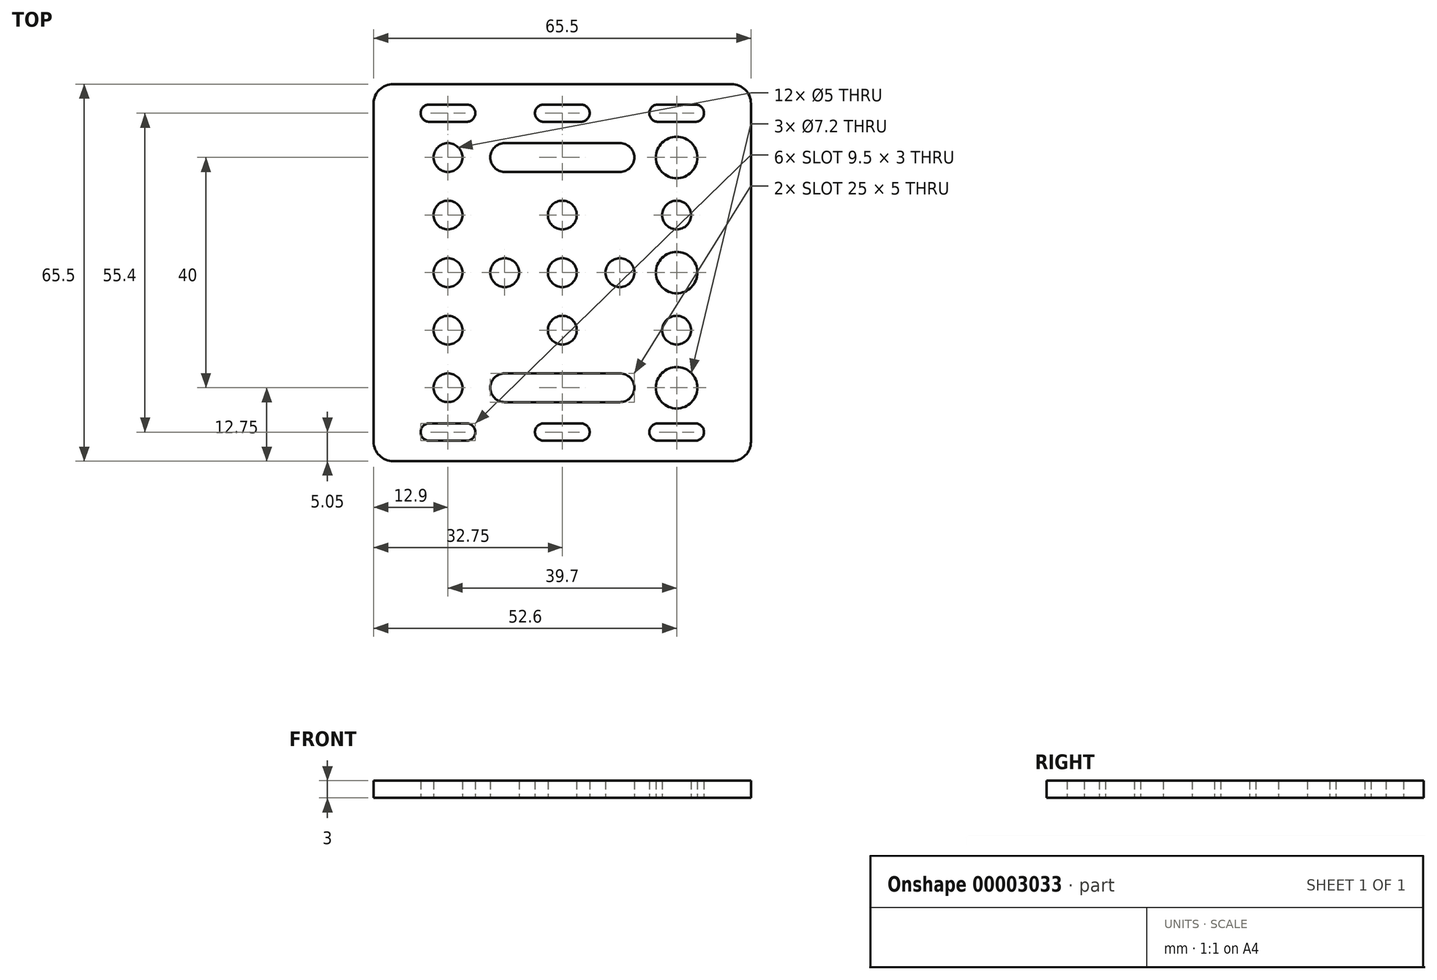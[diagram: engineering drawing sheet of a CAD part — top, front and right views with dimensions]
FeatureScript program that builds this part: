
annotation { "Feature Type Name" : "Feature", "Feature Type Description" : "" }
export const myFeature = defineFeature(function(context is Context, id is Id, definition is map)
    precondition{}
    {
        {
            var Q0;
            Q0=qCreatedBy(makeId("Top.planeOp"),FACE);
            var sketch = newSketch(context, id + "F0", { "sketchPlane" : qUnion([Q0])});
            skLineSegment(sketch, "E0.bottom", {"start": v(3.38, 0) * mm, "end": v(62.12, 0) * mm});
            skLineSegment(sketch, "E0.top", {"start": v(3.38, 65.5) * mm, "end": v(62.12, 65.5) * mm});
            skLineSegment(sketch, "E0.left", {"start": v(0, 3.38) * mm, "end": v(0, 62.12) * mm});
            skLineSegment(sketch, "E0.right", {"start": v(65.5, 3.38) * mm, "end": v(65.5, 62.12) * mm});
            skPoint(sketch, "E1.visualSharp", {"position": v(0, 65.5) * mm});
            skArc(sketch, "E1.filletArc", {"start": v(3.38, 65.5) * mm, "mid": v(0.99, 64.51) * mm, "end": v(0, 62.12) * mm});
            skPoint(sketch, "E2.visualSharp", {"position": v(0, 0) * mm});
            skArc(sketch, "E2.filletArc", {"start": v(0, 3.38) * mm, "mid": v(0.99, 0.99) * mm, "end": v(3.38, 0) * mm});
            skPoint(sketch, "E3.visualSharp", {"position": v(65.5, 0) * mm});
            skArc(sketch, "E3.filletArc", {"start": v(62.12, 0) * mm, "mid": v(64.51, 0.99) * mm, "end": v(65.5, 3.38) * mm});
            skPoint(sketch, "E4.visualSharp", {"position": v(65.5, 65.5) * mm});
            skArc(sketch, "E4.filletArc", {"start": v(65.5, 62.12) * mm, "mid": v(64.51, 64.51) * mm, "end": v(62.12, 65.5) * mm});
            skLineSegment(sketch, "E5", {"start": v(0, 32.75) * mm, "end": v(65.5, 32.75) * mm, "construction": true});
            skCircle(sketch, "E6", {"center": v(12.9, 32.75) * mm, "radius": 2.5 * mm});
            skCircle(sketch, "E7", {"center": v(22.75, 32.75) * mm, "radius": 2.5 * mm});
            skCircle(sketch, "E8", {"center": v(32.75, 32.75) * mm, "radius": 2.5 * mm});
            skCircle(sketch, "E9", {"center": v(52.6, 32.75) * mm, "radius": 3.6 * mm});
            skLineSegment(sketch, "E10", {"start": v(32.75, 65.5) * mm, "end": v(32.75, 0) * mm, "construction": true});
            skCircle(sketch, "E11", {"center": v(42.75, 32.75) * mm, "radius": 2.5 * mm});
            skCircle(sketch, "E12", {"center": v(12.9, 22.75) * mm, "radius": 2.5 * mm});
            skCircle(sketch, "E13", {"center": v(12.9, 12.75) * mm, "radius": 2.5 * mm});
            skCircle(sketch, "E14", {"center": v(32.75, 22.75) * mm, "radius": 2.5 * mm});
            skArc(sketch, "E15", {"start": v(22.75, 15.25) * mm, "mid": v(20.25, 12.75) * mm, "end": v(22.75, 10.25) * mm});
            skArc(sketch, "E16", {"start": v(42.75, 10.25) * mm, "mid": v(45.25, 12.75) * mm, "end": v(42.75, 15.25) * mm});
            skLineSegment(sketch, "E17", {"start": v(22.75, 15.25) * mm, "end": v(42.75, 15.25) * mm});
            skLineSegment(sketch, "E18", {"start": v(22.75, 10.25) * mm, "end": v(42.75, 10.25) * mm});
            skCircle(sketch, "E19", {"center": v(52.6, 12.75) * mm, "radius": 3.6 * mm});
            skCircle(sketch, "E20", {"center": v(52.6, 22.75) * mm, "radius": 2.5 * mm});
            skArc(sketch, "E21", {"start": v(9.65, 6.55) * mm, "mid": v(8.15, 5.05) * mm, "end": v(9.65, 3.55) * mm});
            skArc(sketch, "E22", {"start": v(16.15, 3.55) * mm, "mid": v(17.65, 5.05) * mm, "end": v(16.15, 6.55) * mm});
            skLineSegment(sketch, "E23", {"start": v(9.65, 6.55) * mm, "end": v(16.15, 6.55) * mm});
            skLineSegment(sketch, "E24", {"start": v(9.65, 3.55) * mm, "end": v(16.15, 3.55) * mm});
            skLineSegment(sketch, "E25.0.MirrorCS", {"start": v(55.85, 6.55) * mm, "end": v(49.35, 6.55) * mm});
            skArc(sketch, "E26.0.MirrorCS", {"start": v(49.35, 3.55) * mm, "mid": v(47.85, 5.05) * mm, "end": v(49.35, 6.55) * mm});
            skLineSegment(sketch, "E27.0.MirrorCS", {"start": v(55.85, 3.55) * mm, "end": v(49.35, 3.55) * mm});
            skArc(sketch, "E28.0.MirrorCS", {"start": v(55.85, 6.55) * mm, "mid": v(57.35, 5.05) * mm, "end": v(55.85, 3.55) * mm});
            skArc(sketch, "E29", {"start": v(29.5, 6.55) * mm, "mid": v(28, 5.05) * mm, "end": v(29.5, 3.55) * mm});
            skArc(sketch, "E30", {"start": v(36, 3.55) * mm, "mid": v(37.5, 5.05) * mm, "end": v(36, 6.55) * mm});
            skLineSegment(sketch, "E31", {"start": v(29.5, 6.55) * mm, "end": v(36, 6.55) * mm});
            skLineSegment(sketch, "E32", {"start": v(29.5, 3.55) * mm, "end": v(36, 3.55) * mm});
            skCircle(sketch, "E33.0.MirrorC", {"center": v(12.9, 42.75) * mm, "radius": 2.5 * mm});
            skCircle(sketch, "E34.0.MirrorC", {"center": v(32.75, 42.75) * mm, "radius": 2.5 * mm});
            skCircle(sketch, "E35.0.MirrorC", {"center": v(52.6, 42.75) * mm, "radius": 2.5 * mm});
            skCircle(sketch, "E36.0.MirrorC", {"center": v(52.6, 52.75) * mm, "radius": 3.6 * mm});
            skLineSegment(sketch, "E37.0.MirrorCS", {"start": v(22.75, 55.25) * mm, "end": v(42.75, 55.25) * mm});
            skArc(sketch, "E38.0.MirrorCS", {"start": v(42.75, 55.25) * mm, "mid": v(45.25, 52.75) * mm, "end": v(42.75, 50.25) * mm});
            skLineSegment(sketch, "E39.0.MirrorCS", {"start": v(22.75, 50.25) * mm, "end": v(42.75, 50.25) * mm});
            skArc(sketch, "E40.0.MirrorCS", {"start": v(22.75, 50.25) * mm, "mid": v(20.25, 52.75) * mm, "end": v(22.75, 55.25) * mm});
            skLineSegment(sketch, "E41.0.MirrorCS", {"start": v(9.65, 58.95) * mm, "end": v(16.15, 58.95) * mm});
            skArc(sketch, "E42.0.MirrorCS", {"start": v(16.15, 61.95) * mm, "mid": v(17.65, 60.45) * mm, "end": v(16.15, 58.95) * mm});
            skLineSegment(sketch, "E43.0.MirrorCS", {"start": v(9.65, 61.95) * mm, "end": v(16.15, 61.95) * mm});
            skArc(sketch, "E44.0.MirrorCS", {"start": v(9.65, 58.95) * mm, "mid": v(8.15, 60.45) * mm, "end": v(9.65, 61.95) * mm});
            skArc(sketch, "E45.0.MirrorCS", {"start": v(29.5, 58.95) * mm, "mid": v(28, 60.45) * mm, "end": v(29.5, 61.95) * mm});
            skLineSegment(sketch, "E46.0.MirrorCS", {"start": v(29.5, 58.95) * mm, "end": v(36, 58.95) * mm});
            skArc(sketch, "E47.0.MirrorCS", {"start": v(36, 61.95) * mm, "mid": v(37.5, 60.45) * mm, "end": v(36, 58.95) * mm});
            skLineSegment(sketch, "E48.0.MirrorCS", {"start": v(29.5, 61.95) * mm, "end": v(36, 61.95) * mm});
            skLineSegment(sketch, "E49.0.MirrorCS", {"start": v(55.85, 58.95) * mm, "end": v(49.35, 58.95) * mm});
            skArc(sketch, "E50.0.MirrorCS", {"start": v(49.35, 61.95) * mm, "mid": v(47.85, 60.45) * mm, "end": v(49.35, 58.95) * mm});
            skLineSegment(sketch, "E51.0.MirrorCS", {"start": v(55.85, 61.95) * mm, "end": v(49.35, 61.95) * mm});
            skArc(sketch, "E52.0.MirrorCS", {"start": v(55.85, 58.95) * mm, "mid": v(57.35, 60.45) * mm, "end": v(55.85, 61.95) * mm});
            skCircle(sketch, "E53.0.MirrorC", {"center": v(12.9, 52.75) * mm, "radius": 2.5 * mm});
            skSolve(sketch);
        }
        {
            var Q0;
            Q0=makeQuery(id+"F0.imprint","IMPRINT",FACE,{"disambiguationData":[TD([[makeQuery(id+"F0.imprint","IMPRINT",EDGE,{"derivedFrom":sQuery(id+"F0.wireOp",EDGE,"E0.bottom")}),1.0]])]});
            extrude(context, id + "F1", {"entities" : qUnion([Q0]), "depth" : 3 * mm});
        }
    });
